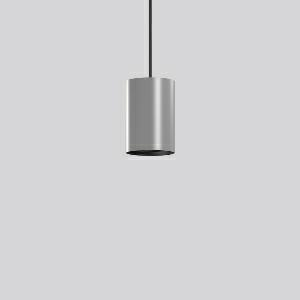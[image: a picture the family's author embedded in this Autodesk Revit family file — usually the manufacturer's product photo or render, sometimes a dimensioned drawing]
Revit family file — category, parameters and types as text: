
# Revit family: deecos_p_maxi_911544_004_c17c
name_source: partatom
category: Lighting Fixtures
units: mm (PartAtom-declared; Revit-internal decimal feet)

## family parameters
Cut with Voids When Loaded = No
Host = Face
Light Source = No
Part Type = Normal
Room Calculation Point = No
Round Connector Dimension = Use Diameter
Shared = No

## types (1)
- DEECOS P maxi (1 x LED Modul 932 fresh meat, 2150 lm, 3200)
    Apparent Load = 33 VA
    Approval mark = CE
    CIE Flux Codes = 100 100 100 100 100
    Color Rendering = 90
    Color Temperature = 3200
    Default Elevation = 1800 mm
    Description = Series: DEECOS P maxi
Cylindrical pendant luminaire. Housing: die-cast aluminium, powder-coated. Canopy made of powder-coated sheet steel with magnetic attachment. Optical assembly with reflector made of MIRO-Silver with 98% total light reflection for outstanding efficiency - can be changed without tools. Including special LED for illuminating meat products / Meat fresh - reddish white. Transparent suspension cable 2 m, can be shortened. High quality converter without flickering and stroboscopic effect. The following accessories can be mounted without use of tools: interchangeable lenses, honeycomb louvre, clear and frosted diffusers, white interchangeable plastic ring. Decorative recessed suspension set available as accessory. 
Colour: silver
Diameter: 123 mm
Height: 181 mm
Suspension length: 2000 mm
Lamp: LED
Socket: without socket
Colour temperature: fresh meat
Colour rendering index (CRI): 92
System power: 33 W
Rated luminous flux: 2150 lm
Luminous efficiency: 65 lm/W
Control gear: Regulated power supply
Protection class: I
Type of protection: IP 20
    Height = 181 mm
    Lamp = 1 x LED Modul 932 fresh meat
    Lamp Light Flux = 2150 lm
    Lamp count = 1
    Length = 123 mm
    Lifetime = 50000 h
    Luminous efficacy = 65 lm/W
    Manufacturer = RZB
    ModVariant = No
    Model = 911544.004
    Mounting Place = Ceiling
    Mounting Type = Pendant
    Number of Poles = 1
    OnlyDefault = Yes
    Power Factor = 1
    Product Name = DEECOS P maxi
    Product group = Pendant luminaires
    ProductGroupID = 902
    Protection Class = Protection class I
    Protection Degree = IP 20
    RLX_Detail_Level = 1
    RLX_Emergency_Light_Flux = 0 lm
    RLX_Emergency_Type = 0
    RLX_Emergency_Type_DB = No
    RlxData = <blob elided: 36137 chars, md5=fa12d24a>
    Socket = socket
    Standby Power = 0 W
    System Light Flux = 2150 lm
    System Power = 33 W
    Type Comments = Product without accessories
    Type Image = 911480.004.jpg
    URL = http://relux.com
    VarID = ---
    Voltage = 230 V
    Voltage Range = 220-240 V
    Weight = 0.00 kg
    Width = 0 mm  [stored 0 ft]

note: [stored X ft] marks values corroborated as IEEE doubles in the binary element streams (Revit-internal decimal feet)

## geometry (parser evidence)
native form markers: Blend x4, Sweep x8
no freeform markers — native parametric forms only
